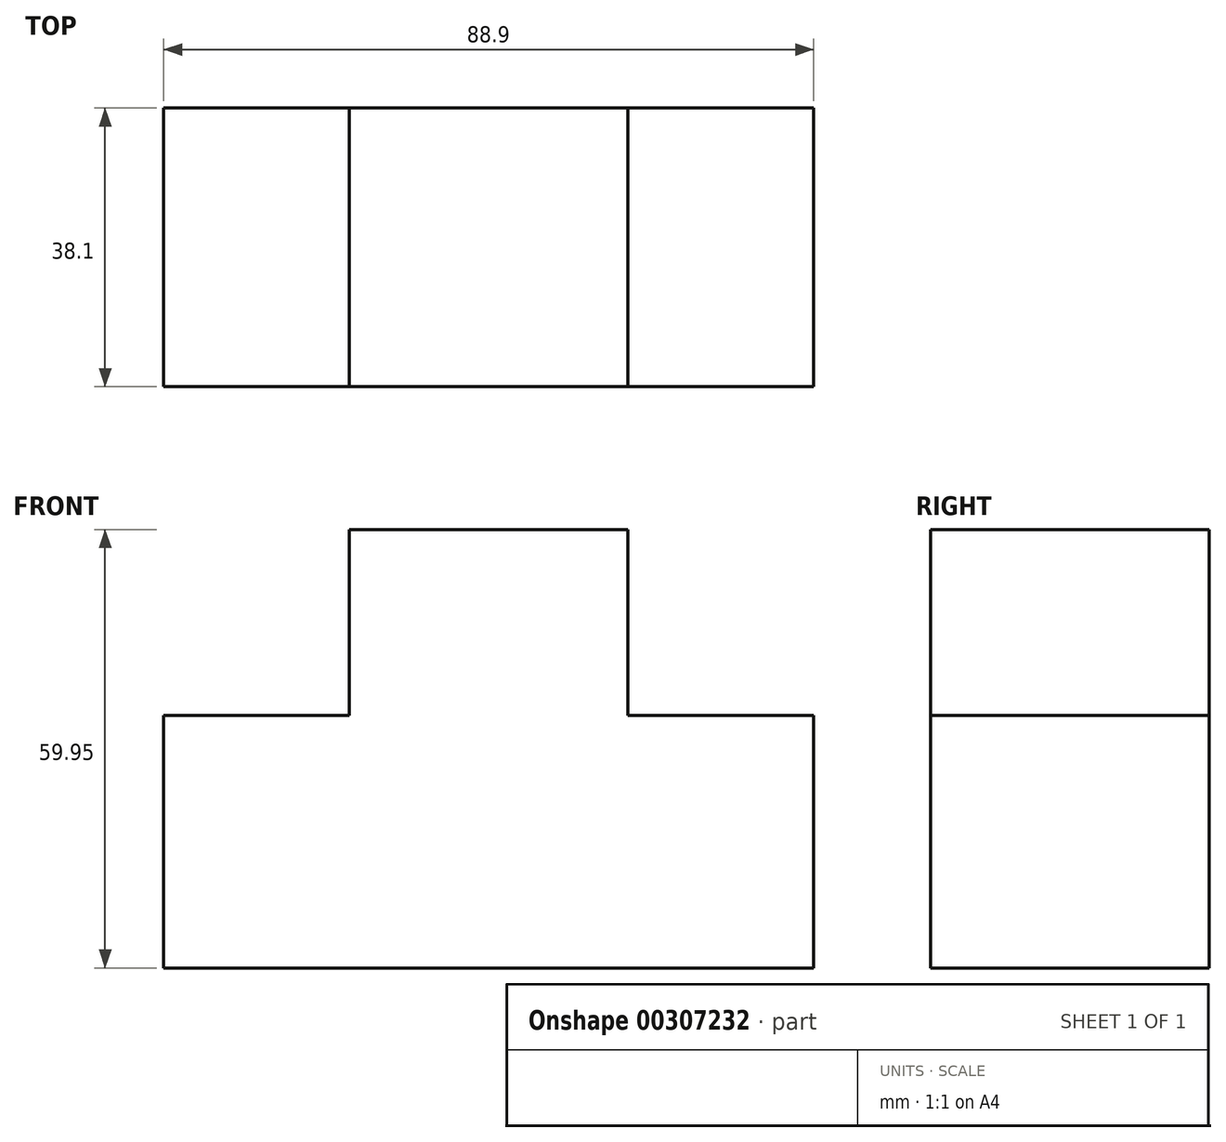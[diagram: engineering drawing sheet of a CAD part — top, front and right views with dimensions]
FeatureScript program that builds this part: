
annotation { "Feature Type Name" : "Feature", "Feature Type Description" : "" }
export const myFeature = defineFeature(function(context is Context, id is Id, definition is map)
    precondition{}
    {
        {
            var Q0;
            Q0=qCreatedBy(makeId("Front.planeOp"),FACE);
            var sketch = newSketch(context, id + "F0", { "sketchPlane" : qUnion([Q0])});
            skLineSegment(sketch, "E0", {"start": v(-54.82, -43.78) * mm, "end": v(34.08, -43.78) * mm});
            skLineSegment(sketch, "E1", {"start": v(34.08, -43.78) * mm, "end": v(34.08, -9.23) * mm});
            skLineSegment(sketch, "E2", {"start": v(34.08, -9.23) * mm, "end": v(8.68, -9.23) * mm});
            skLineSegment(sketch, "E3", {"start": v(8.68, -9.23) * mm, "end": v(8.68, 16.17) * mm});
            skLineSegment(sketch, "E4", {"start": v(8.68, 16.17) * mm, "end": v(-29.42, 16.17) * mm});
            skLineSegment(sketch, "E5", {"start": v(-29.42, 16.17) * mm, "end": v(-29.42, -9.23) * mm});
            skLineSegment(sketch, "E6", {"start": v(-29.42, -9.23) * mm, "end": v(-54.82, -9.23) * mm});
            skLineSegment(sketch, "E7", {"start": v(-54.82, -9.23) * mm, "end": v(-54.82, -43.78) * mm});
            skSolve(sketch);
        }
        {
            var Q0;
            Q0=makeQuery(id+"F0.imprint","IMPRINT",FACE,{"disambiguationData":[TD([[makeQuery(id+"F0.imprint","IMPRINT",EDGE,{"derivedFrom":sQuery(id+"F0.wireOp",EDGE,"E0")}),1.0]])]});
            extrude(context, id + "F1", {"entities" : qUnion([Q0]), "depth" : 38.1 * mm});
        }
    });
